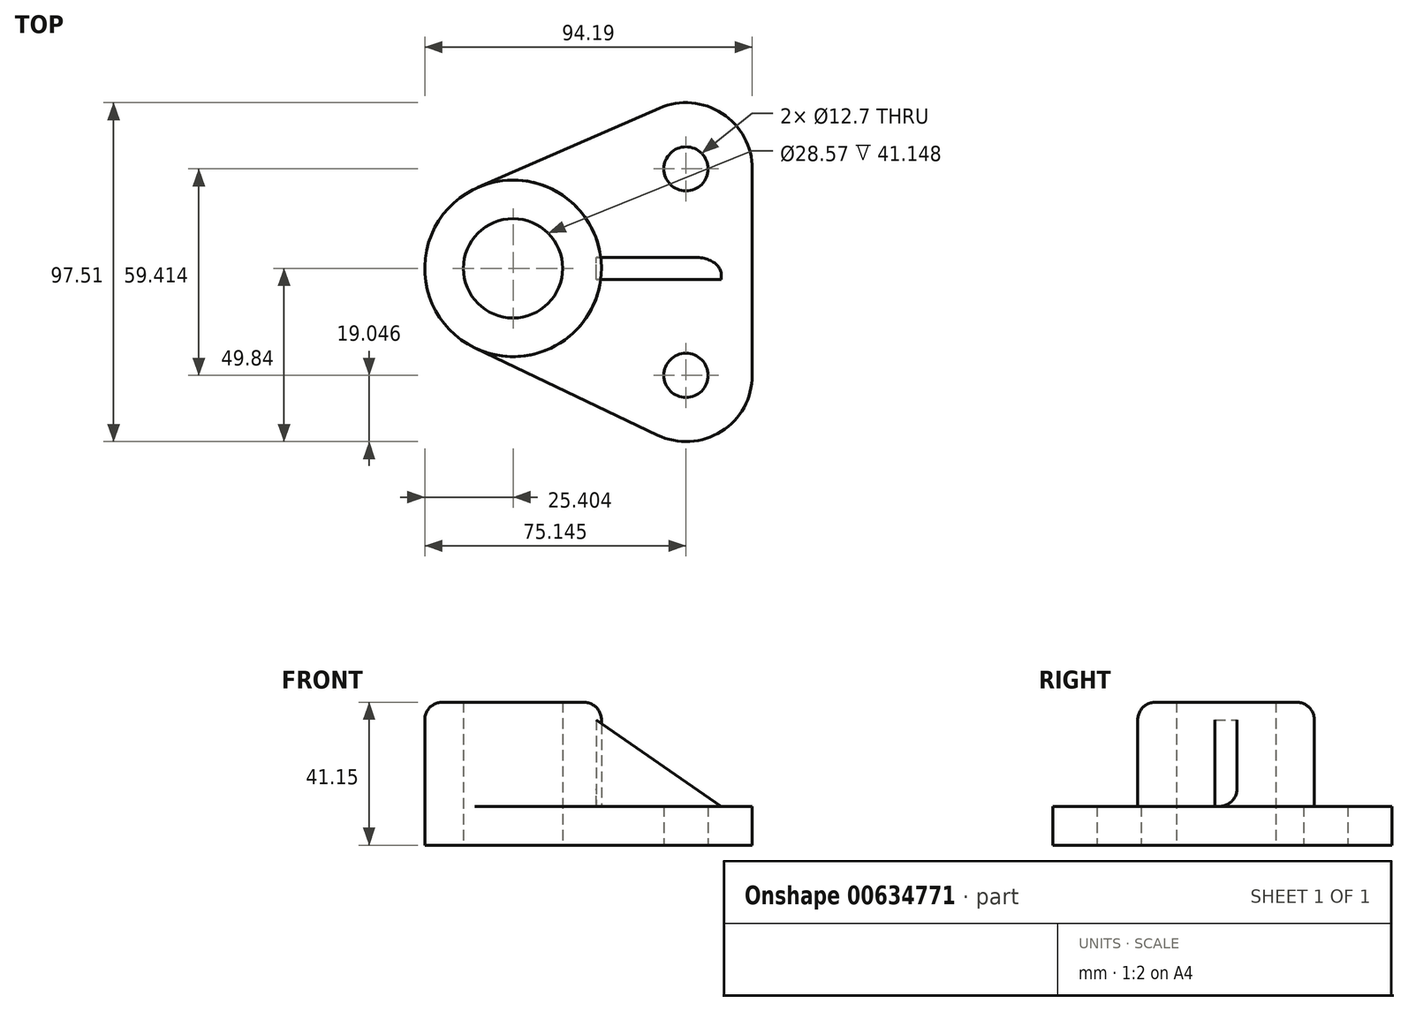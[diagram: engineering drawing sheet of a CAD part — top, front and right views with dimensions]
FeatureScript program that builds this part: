
annotation { "Feature Type Name" : "Feature", "Feature Type Description" : "" }
export const myFeature = defineFeature(function(context is Context, id is Id, definition is map)
    precondition{}
    {
        {
            var Q0;
            Q0=qCreatedBy(makeId("Top.planeOp"),FACE);
            var sketch = newSketch(context, id + "F0", { "sketchPlane" : qUnion([Q0])});
            skLineSegment(sketch, "E0", {"start": v(-26.42, 0) * mm, "end": v(23.32, 0) * mm});
            skLineSegment(sketch, "E1", {"start": v(23.32, 0) * mm, "end": v(23.32, 28.62) * mm});
            skLineSegment(sketch, "E2", {"start": v(23.32, 0) * mm, "end": v(23.32, -30.8) * mm});
            skCircle(sketch, "E3", {"center": v(-26.42, 0) * mm, "radius": 14.29 * mm});
            skCircle(sketch, "E4", {"center": v(-26.42, 0) * mm, "radius": 25.4 * mm});
            skCircle(sketch, "E5", {"center": v(23.32, -30.8) * mm, "radius": 19.05 * mm});
            skCircle(sketch, "E6", {"center": v(23.32, 28.62) * mm, "radius": 19.05 * mm});
            skCircle(sketch, "E7", {"center": v(23.32, -30.8) * mm, "radius": 6.35 * mm});
            skCircle(sketch, "E8", {"center": v(23.32, 28.62) * mm, "radius": 6.35 * mm});
            skLineSegment(sketch, "E9", {"start": v(-36.57, 23.28) * mm, "end": v(15.7, 46.08) * mm});
            skLineSegment(sketch, "E10", {"start": v(-37.36, -22.92) * mm, "end": v(15.11, -47.98) * mm});
            skLineSegment(sketch, "E11", {"start": v(42.37, 28.62) * mm, "end": v(42.37, -30.8) * mm});
            skSolve(sketch);
        }
        {
            var Q0;
            Q0=makeQuery(id+"F0.imprint","IMPRINT",FACE,{"disambiguationData":[TD([[makeQuery(id+"F0.imprint","IMPRINT",EDGE,{"derivedFrom":sQuery(id+"F0.wireOp",EDGE,"E3")}),-1.0]])]});
            extrude(context, id + "F1", {"entities" : qUnion([Q0]), "depth" : 41.15 * mm, "offsetDistance" : 25.4 * mm});
        }
        {
            var Q0;
            {var subQ0=sQuery(id+"F0.wireOp",EDGE,"E11");Q0=makeQuery(id+"F0.imprint","IMPRINT",FACE,{"disambiguationData":[TD([[makeQuery(id+"F0.imprint","IMPRINT",EDGE,{"derivedFrom":subQ0}),-1.0]])]});}
            var Q1;
            {var subQ0=sQuery(id+"F0.wireOp",EDGE,"E10");Q1=makeQuery(id+"F0.imprint","IMPRINT",FACE,{"disambiguationData":[TD([[makeQuery(id+"F0.imprint","IMPRINT",EDGE,{"derivedFrom":subQ0}),1.0]])]});}
            var Q2;
            Q2=makeQuery(id+"F0.imprint","IMPRINT",FACE,{"disambiguationData":[TD([[makeQuery(id+"F0.imprint","IMPRINT",EDGE,{"derivedFrom":sQuery(id+"F0.wireOp",EDGE,"E7")}),-1.0]])]});
            var Q3;
            {var subQ0=sQuery(id+"F0.wireOp",EDGE,"E9");Q3=makeQuery(id+"F0.imprint","IMPRINT",FACE,{"disambiguationData":[TD([[makeQuery(id+"F0.imprint","IMPRINT",EDGE,{"derivedFrom":subQ0}),-1.0]])]});}
            var Q4;
            Q4=makeQuery(id+"F0.imprint","IMPRINT",FACE,{"disambiguationData":[TD([[makeQuery(id+"F0.imprint","IMPRINT",EDGE,{"derivedFrom":sQuery(id+"F0.wireOp",EDGE,"E8")}),-1.0]])]});
            extrude(context, id + "F2", {"entities" : qUnion([Q0, Q1, Q2, Q3, Q4]), "operationType" : NewBodyOperationType.ADD, "depth" : 11.18 * mm, "offsetDistance" : 25.4 * mm});
        }
        {
            var Q0;
            Q0=qCreatedBy(makeId("Front.planeOp"),FACE);
            var sketch = newSketch(context, id + "F3", { "sketchPlane" : qUnion([Q0])});
            skPoint(sketch, "E12.0", {"position": v(33.49, 11.18) * mm});
            skLineSegment(sketch, "E13", {"start": v(33.49, 11.18) * mm, "end": v(-2.52, 36.06) * mm});
            skLineSegment(sketch, "E14", {"start": v(-2.52, 36.06) * mm, "end": v(-2.52, 11.18) * mm});
            skLineSegment(sketch, "E15", {"start": v(-2.52, 11.18) * mm, "end": v(33.49, 11.18) * mm});
            skSolve(sketch);
        }
        {
            var Q0;
            Q0=makeQuery(id+"F1.opExtrude","CAP_EDGE",EDGE,{"disambiguationData":[OSD([sQuery(id+"F0.wireOp",EDGE,"E4")])],"isStart":false});
            fillet(context, id + "F4", {"entities" : qUnion([Q0]), "radius" : 5.08 * mm, "tangentPropagation" : true, "allowEdgeOverflow" : false});
        }
        {
            var Q0;
            Q0 = qSketchRegion(id + "F3", true);
            extrude(context, id + "F5", {"entities" : qUnion([Q0]), "endBound" : BoundingType.SYMMETRIC, "depth" : 6.35 * mm, "offsetDistance" : 25.4 * mm});
        }
        {
            var Q0;
            Q0=makeQuery(id+"F2.opExtrude","CAP_EDGE",EDGE,{"disambiguationData":[OSD([sQuery(id+"F0.wireOp",EDGE,"E4")])],"isStart":false});
            var Q1;
            Q1=makeQuery(id+"F5.opExtrude","CAP_EDGE",EDGE,{"disambiguationData":[OSD([sQuery(id+"F3.wireOp",EDGE,"E15")])],"isStart":true});
            fillet(context, id + "F6", {"entities" : qUnion([Q0, Q1]), "radius" : 5.08 * mm, "tangentPropagation" : true, "allowEdgeOverflow" : false});
        }
    });
